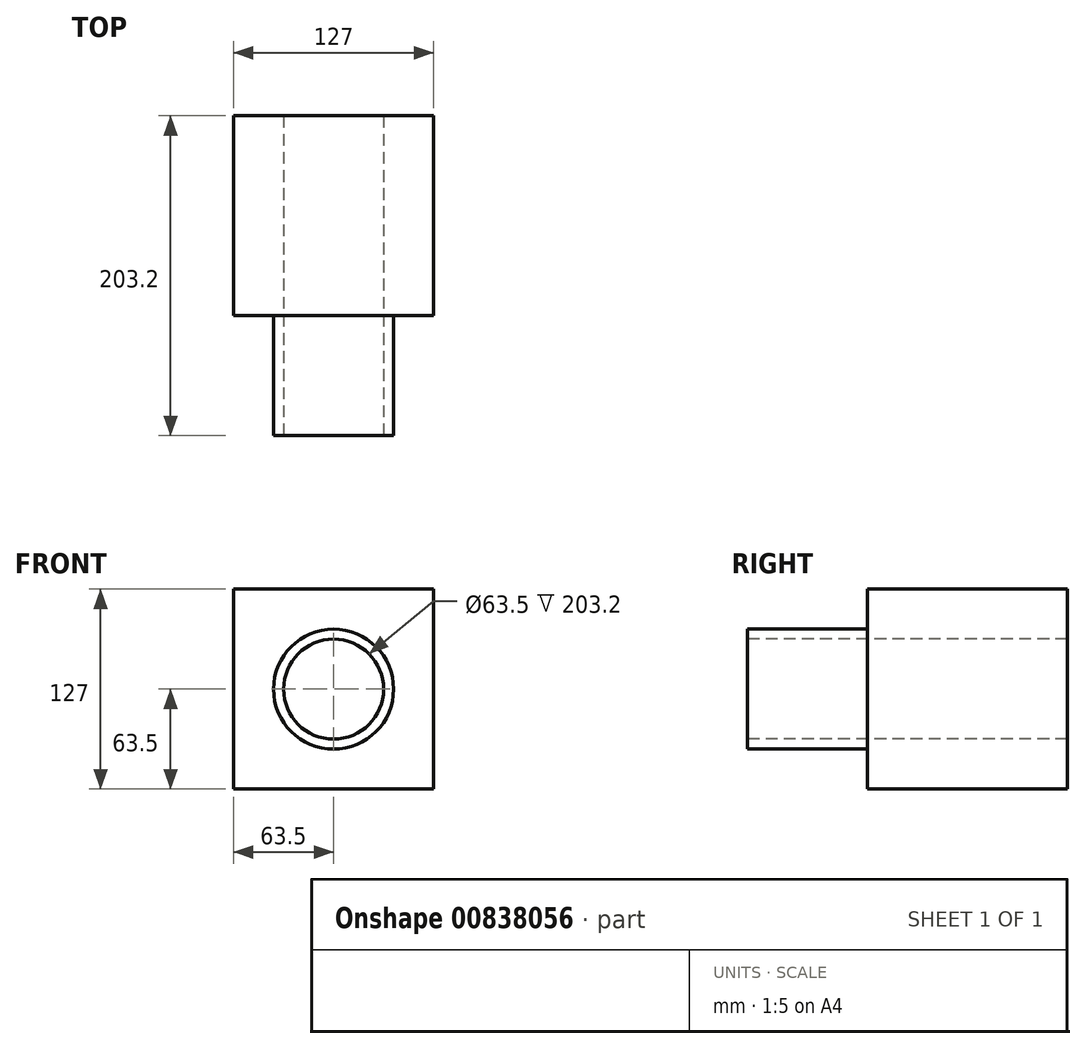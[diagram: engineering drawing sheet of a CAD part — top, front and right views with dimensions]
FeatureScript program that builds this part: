
annotation { "Feature Type Name" : "Feature", "Feature Type Description" : "" }
export const myFeature = defineFeature(function(context is Context, id is Id, definition is map)
    precondition{}
    {
        {
            var Q0;
            Q0=qCreatedBy(makeId("Front.planeOp"),FACE);
            var sketch = newSketch(context, id + "F0", { "sketchPlane" : qUnion([Q0])});
            skLineSegment(sketch, "E0.bottom", {"start": v(63.5, 63.5) * mm, "end": v(-63.5, 63.5) * mm});
            skLineSegment(sketch, "E0.top", {"start": v(63.5, -63.5) * mm, "end": v(-63.5, -63.5) * mm});
            skLineSegment(sketch, "E0.left", {"start": v(63.5, 63.5) * mm, "end": v(63.5, -63.5) * mm});
            skLineSegment(sketch, "E0.right", {"start": v(-63.5, 63.5) * mm, "end": v(-63.5, -63.5) * mm});
            skPoint(sketch, "E0.middle", {"position": v(0, 0) * mm});
            skSolve(sketch);
        }
        {
            var Q0;
            Q0=makeQuery(id+"F0.imprint","IMPRINT",FACE,{"disambiguationData":[TD([[makeQuery(id+"F0.imprint","IMPRINT",EDGE,{"derivedFrom":sQuery(id+"F0.wireOp",EDGE,"E0.bottom")}),1.0]])]});
            extrude(context, id + "F1", {"entities" : qUnion([Q0]), "depth" : 127 * mm, "offsetDistance" : 25.4 * mm});
        }
        {
            var Q0;
            Q0=makeQuery(id+"F1.opExtrude","CAP_FACE",FACE,{"disambiguationData":[OSD([sQuery(id+"F0.wireOp",EDGE,"E0.bottom"),sQuery(id+"F0.wireOp",EDGE,"E0.top"),sQuery(id+"F0.wireOp",EDGE,"E0.left"),sQuery(id+"F0.wireOp",EDGE,"E0.right")])],"isStart":false});
            var sketch = newSketch(context, id + "F2", { "sketchPlane" : qUnion([Q0])});
            skCircle(sketch, "E1", {"center": v(0, 0) * mm, "radius": 31.75 * mm});
            skSolve(sketch);
        }
        {
            var Q0;
            Q0=makeQuery(id+"F2.imprint","IMPRINT",FACE,{"disambiguationData":[TD([[makeQuery(id+"F2.imprint","IMPRINT",EDGE,{"derivedFrom":sQuery(id+"F2.wireOp",EDGE,"E1")}),1.0]])]});
            extrude(context, id + "F3", {"entities" : qUnion([Q0]), "operationType" : NewBodyOperationType.REMOVE, "endBound" : BoundingType.THROUGH_ALL, "oppositeDirection" : true, "depth" : 25.4 * mm, "offsetDistance" : 25.4 * mm});
        }
        {
            var Q0;
            Q0=makeQuery(id+"F1.opExtrude","CAP_FACE",FACE,{"disambiguationData":[OSD([sQuery(id+"F0.wireOp",EDGE,"E0.bottom"),sQuery(id+"F0.wireOp",EDGE,"E0.top"),sQuery(id+"F0.wireOp",EDGE,"E0.left"),sQuery(id+"F0.wireOp",EDGE,"E0.right")])],"isStart":false});
            var sketch = newSketch(context, id + "F4", { "sketchPlane" : qUnion([Q0])});
            skCircle(sketch, "E2", {"center": v(0, 0) * mm, "radius": 38.1 * mm});
            skSolve(sketch);
        }
        {
            var Q0;
            Q0=makeQuery(id+"F4.imprint","IMPRINT",FACE,{"disambiguationData":[TD([[makeQuery(id+"F4.imprint","IMPRINT",EDGE,{"derivedFrom":sQuery(id+"F4.wireOp",EDGE,"E2")}),1.0]])]});
            extrude(context, id + "F5", {"entities" : qUnion([Q0]), "operationType" : NewBodyOperationType.ADD, "depth" : 76.2 * mm, "offsetDistance" : 25.4 * mm});
        }
    });
